# Revit family: DC_Rheem_PLM_Raypak_B1182ID
name_source: partatom
category: Plumbing Fixtures
units: mm (PartAtom-declared; Revit-internal decimal feet)

## family parameters
Cut with Voids When Loaded = No
Host = Face
Part Type = Normal
Room Calculation Point = No
Round Connector Dimension = Use Radius
Shared = No

## types (4) — shared parameters
BoxHeight_ANZRS = 860 mm  [stored 2.82152 ft]
ColdWaterInletDiameter_ANZRS = 65 mm
ColdWaterInletRadius_ANZRS = 33 mm
ConnectionHeight_ANZRS = 755 mm
GasInletHeight_ANZRS = 410 mm
Height_ANZRS = 1915 mm
Manufacturer = Raypak
Materials_ANZRS = Raypak - Grey Powder Coated Steel
PRV_ANZRS = 15 mm  [stored 0.0492126 ft]
URL = http://www.rheem.com.au
Width_ANZRS = 825 mm  [stored 2.70669 ft]
zero-valued in all types: Default Elevation

## per-type parameters (varying)
| type | GasInletDiameter_ANZRS | GasInletRadius_ANZRS | HotWaterOutletDiameter_ANZRS | HotWaterOutletRadius_ANZRS | Model | Type Comments |
| Raypak - Gas Water Heater- Indoor - 1186 MJ/h  Natural gas, modulating gas control | 40 mm | 20 mm  [stored 0.0656168 ft] | 65 mm | 33 mm | B1182NCM/ID | Recovery 4558L/h @ 50°C rise |
| Raypak - Gas Water Heater- Indoor - 1186 MJ/h  Natural gas, On/Off gas control | 40 mm | 20 mm  [stored 0.0656168 ft] | 65 mm | 33 mm | B1182NCO/ID | Recovery 4558L/h @ 50°C rise |
| Raypak - Gas Water Heater- Indoor - 1090 MJ/h  Propane gas, modulating gas control | 20 mm  [stored 0.0656168 ft] | 10 mm  [stored 0.0328084 ft] | 64 mm | 32 mm  [stored 0.104987 ft] | B1182PCM/ID | Recovery 4128L/h @ 50°C rise |
| Raypak - Gas Water Heater- Indoor - 1090 MJ/h  Propane gas, On/Off gas control | 32 mm  [stored 0.104987 ft] | 16 mm  [stored 0.0524934 ft] | 65 mm | 33 mm | B1182PCO/ID | Recovery 4128L/h @ 50°C rise |

note: column(s) folded — value = type name in every type: Description

note: [stored X ft] marks values corroborated as IEEE doubles in the binary element streams (Revit-internal decimal feet)

## geometry (parser evidence)
native form markers: Blend x6, Sweep x2
no freeform markers — native parametric forms only
